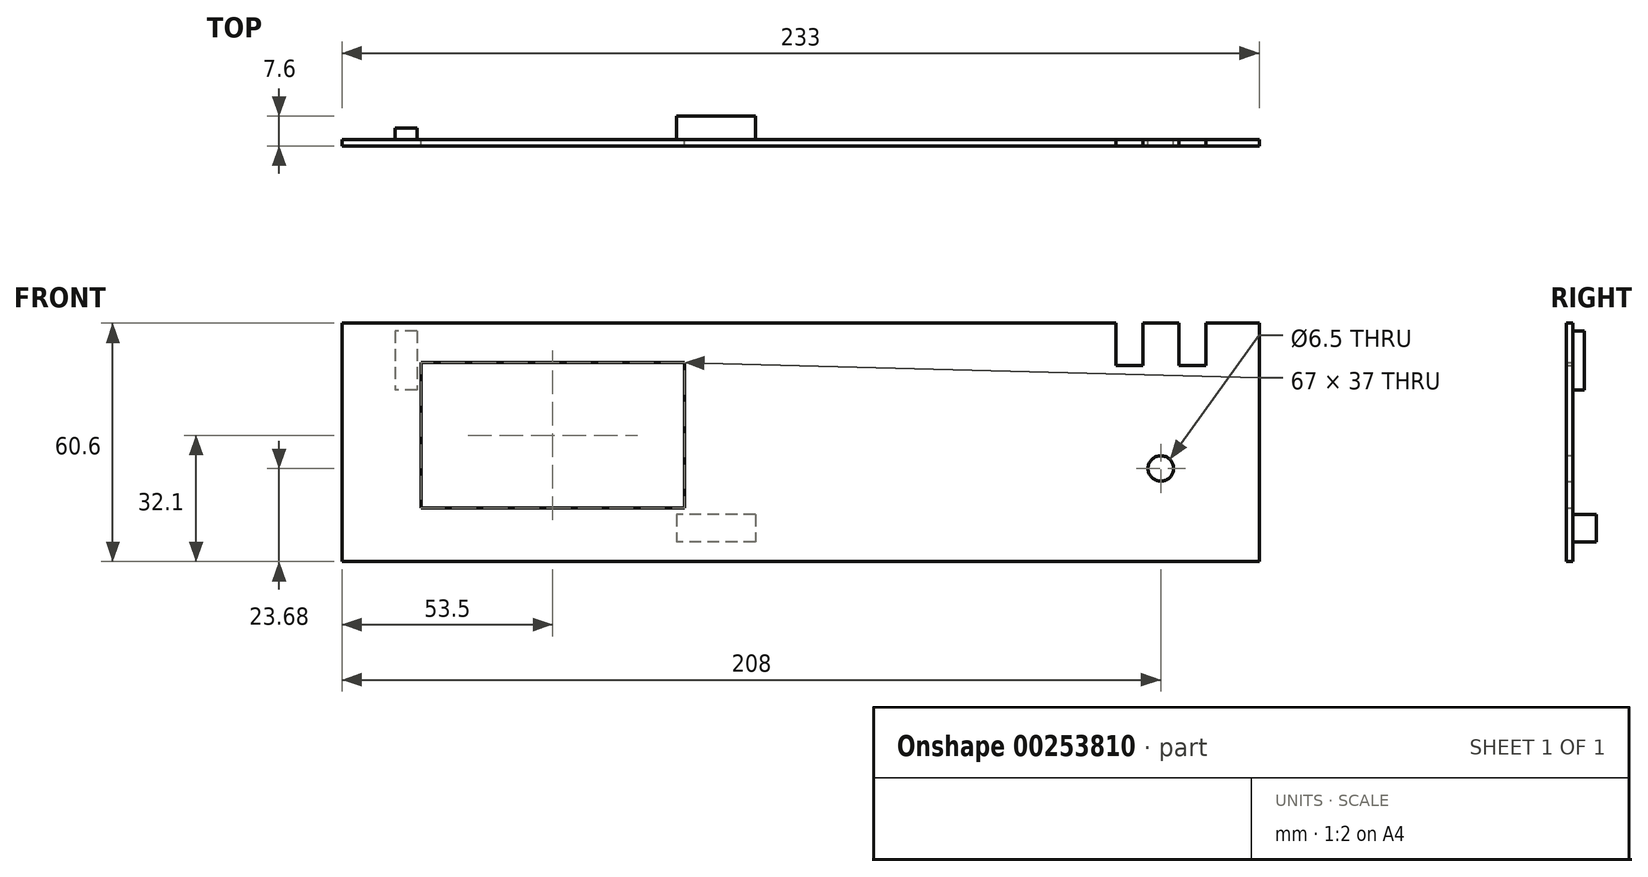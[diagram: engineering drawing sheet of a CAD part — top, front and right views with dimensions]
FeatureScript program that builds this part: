
annotation { "Feature Type Name" : "Feature", "Feature Type Description" : "" }
export const myFeature = defineFeature(function(context is Context, id is Id, definition is map)
    precondition{}
    {
        {
            var Q0;
            Q0=qCreatedBy(makeId("Front.planeOp"),FACE);
            var sketch = newSketch(context, id + "F0", { "sketchPlane" : qUnion([Q0])});
            skLineSegment(sketch, "E0.bottom", {"start": v(116.5, -30.3) * mm, "end": v(-116.5, -30.3) * mm});
            skLineSegment(sketch, "E0.top", {"start": v(116.5, 30.3) * mm, "end": v(-116.5, 30.3) * mm});
            skLineSegment(sketch, "E0.left", {"start": v(116.5, -30.3) * mm, "end": v(116.5, 30.3) * mm});
            skLineSegment(sketch, "E0.right", {"start": v(-116.5, -30.3) * mm, "end": v(-116.5, 30.3) * mm});
            skPoint(sketch, "E0.middle", {"position": v(0, 0) * mm});
            skLineSegment(sketch, "E1.bottom", {"start": v(-96.5, 20.3) * mm, "end": v(-29.5, 20.3) * mm});
            skLineSegment(sketch, "E1.top", {"start": v(-96.5, -16.7) * mm, "end": v(-29.5, -16.7) * mm});
            skLineSegment(sketch, "E1.left", {"start": v(-96.5, 20.3) * mm, "end": v(-96.5, -16.7) * mm});
            skLineSegment(sketch, "E1.right", {"start": v(-29.5, 20.3) * mm, "end": v(-29.5, -16.7) * mm});
            skCircle(sketch, "E2", {"center": v(91.5, -6.62) * mm, "radius": 3.25 * mm});
            skLineSegment(sketch, "E3.bottom", {"start": v(96.1, 30.3) * mm, "end": v(102.9, 30.3) * mm});
            skLineSegment(sketch, "E3.top", {"start": v(96.1, 19.57) * mm, "end": v(102.9, 19.57) * mm});
            skLineSegment(sketch, "E3.left", {"start": v(96.1, 30.3) * mm, "end": v(96.1, 19.57) * mm});
            skLineSegment(sketch, "E3.right", {"start": v(102.9, 30.3) * mm, "end": v(102.9, 19.57) * mm});
            skLineSegment(sketch, "E4.bottom", {"start": v(80.1, 30.3) * mm, "end": v(86.9, 30.3) * mm});
            skLineSegment(sketch, "E4.top", {"start": v(80.1, 19.57) * mm, "end": v(86.9, 19.57) * mm});
            skLineSegment(sketch, "E4.left", {"start": v(80.1, 30.3) * mm, "end": v(80.1, 19.57) * mm});
            skLineSegment(sketch, "E4.right", {"start": v(86.9, 30.3) * mm, "end": v(86.9, 19.57) * mm});
            skPoint(sketch, "E5", {"position": v(83.5, 19.57) * mm});
            skPoint(sketch, "E6", {"position": v(99.5, 19.57) * mm});
            skSolve(sketch);
        }
        {
            var Q0;
            Q0=makeQuery(id+"F0.imprint","IMPRINT",FACE,{"disambiguationData":[TD([[makeQuery(id+"F0.imprint","IMPRINT",EDGE,{"derivedFrom":sQuery(id+"F0.wireOp",EDGE,"E0.bottom")}),-1.0]])]});
            extrude(context, id + "F1", {"entities" : qUnion([Q0]), "depth" : 1.6 * mm});
        }
        {
            var Q0;
            Q0=makeQuery(id+"F1.opExtrude","CAP_FACE",FACE,{"disambiguationData":[OSD([sQuery(id+"F0.wireOp",EDGE,"E0.bottom"),sQuery(id+"F0.wireOp",EDGE,"E0.top"),sQuery(id+"F0.wireOp",EDGE,"E0.left"),sQuery(id+"F0.wireOp",EDGE,"E0.right"),sQuery(id+"F0.wireOp",EDGE,"E1.bottom"),sQuery(id+"F0.wireOp",EDGE,"E1.top"),sQuery(id+"F0.wireOp",EDGE,"E1.left"),sQuery(id+"F0.wireOp",EDGE,"E1.right"),sQuery(id+"F0.wireOp",EDGE,"E2"),sQuery(id+"F0.wireOp",EDGE,"E3.top"),sQuery(id+"F0.wireOp",EDGE,"E3.left"),sQuery(id+"F0.wireOp",EDGE,"E3.right"),sQuery(id+"F0.wireOp",EDGE,"E4.top"),sQuery(id+"F0.wireOp",EDGE,"E4.left"),sQuery(id+"F0.wireOp",EDGE,"E4.right")])],"isStart":true});
            var sketch = newSketch(context, id + "F2", { "sketchPlane" : qUnion([Q0])});
            skLineSegment(sketch, "E7.bottom", {"start": v(11.5, -18.3) * mm, "end": v(31.5, -18.3) * mm});
            skLineSegment(sketch, "E7.top", {"start": v(11.5, -25.3) * mm, "end": v(31.5, -25.3) * mm});
            skLineSegment(sketch, "E7.left", {"start": v(11.5, -18.3) * mm, "end": v(11.5, -25.3) * mm});
            skLineSegment(sketch, "E7.right", {"start": v(31.5, -18.3) * mm, "end": v(31.5, -25.3) * mm});
            skSolve(sketch);
        }
        {
            var Q0;
            Q0 = qSketchRegion(id + "F2", true);
            extrude(context, id + "F3", {"entities" : qUnion([Q0]), "operationType" : NewBodyOperationType.ADD, "depth" : 6 * mm, "offsetDistance" : 25 * mm});
        }
        {
            var Q0;
            Q0=makeQuery(id+"F1.opExtrude","CAP_FACE",FACE,{"disambiguationData":[OSD([sQuery(id+"F0.wireOp",EDGE,"E0.bottom"),sQuery(id+"F0.wireOp",EDGE,"E0.top"),sQuery(id+"F0.wireOp",EDGE,"E0.left"),sQuery(id+"F0.wireOp",EDGE,"E0.right"),sQuery(id+"F0.wireOp",EDGE,"E1.bottom"),sQuery(id+"F0.wireOp",EDGE,"E1.top"),sQuery(id+"F0.wireOp",EDGE,"E1.left"),sQuery(id+"F0.wireOp",EDGE,"E1.right"),sQuery(id+"F0.wireOp",EDGE,"E2"),sQuery(id+"F0.wireOp",EDGE,"E3.top"),sQuery(id+"F0.wireOp",EDGE,"E3.left"),sQuery(id+"F0.wireOp",EDGE,"E3.right"),sQuery(id+"F0.wireOp",EDGE,"E4.top"),sQuery(id+"F0.wireOp",EDGE,"E4.left"),sQuery(id+"F0.wireOp",EDGE,"E4.right")])],"isStart":true});
            var sketch = newSketch(context, id + "F4", { "sketchPlane" : qUnion([Q0])});
            skLineSegment(sketch, "E8.bottom", {"start": v(97.5, 28.3) * mm, "end": v(103, 28.3) * mm});
            skLineSegment(sketch, "E8.top", {"start": v(97.5, 13.3) * mm, "end": v(103, 13.3) * mm});
            skLineSegment(sketch, "E8.left", {"start": v(97.5, 28.3) * mm, "end": v(97.5, 13.3) * mm});
            skLineSegment(sketch, "E8.right", {"start": v(103, 28.3) * mm, "end": v(103, 13.3) * mm});
            skSolve(sketch);
        }
        {
            var Q0;
            Q0 = qSketchRegion(id + "F4", true);
            extrude(context, id + "F5", {"entities" : qUnion([Q0]), "operationType" : NewBodyOperationType.ADD, "depth" : 3 * mm, "offsetDistance" : 25 * mm});
        }
    });
